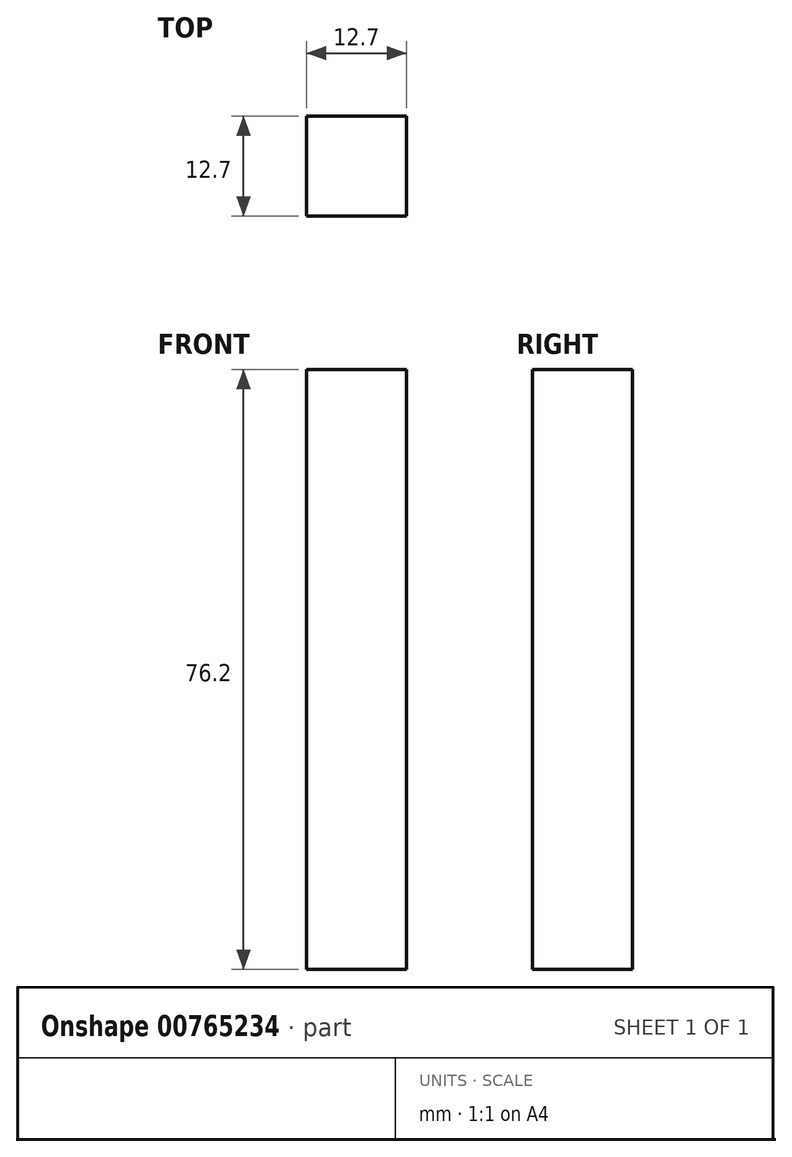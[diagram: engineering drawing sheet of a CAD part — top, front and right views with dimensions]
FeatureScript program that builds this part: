
annotation { "Feature Type Name" : "Feature", "Feature Type Description" : "" }
export const myFeature = defineFeature(function(context is Context, id is Id, definition is map)
    precondition{}
    {
        {
            var Q0;
            Q0=qCreatedBy(makeId("Front.planeOp"),FACE);
            var sketch = newSketch(context, id + "F0", { "sketchPlane" : qUnion([Q0])});
            skLineSegment(sketch, "E0.bottom", {"start": v(6.35, 38.1) * mm, "end": v(-6.35, 38.1) * mm});
            skLineSegment(sketch, "E0.top", {"start": v(6.35, -38.1) * mm, "end": v(-6.35, -38.1) * mm});
            skLineSegment(sketch, "E0.left", {"start": v(6.35, 38.1) * mm, "end": v(6.35, -38.1) * mm});
            skLineSegment(sketch, "E0.right", {"start": v(-6.35, 38.1) * mm, "end": v(-6.35, -38.1) * mm});
            skPoint(sketch, "E0.middle", {"position": v(0, 0) * mm});
            skSolve(sketch);
        }
        {
            var Q0;
            Q0 = qSketchRegion(id + "F0", true);
            extrude(context, id + "F1", {"entities" : qUnion([Q0]), "depth" : 12.7 * mm, "offsetDistance" : 25.4 * mm});
        }
    });
